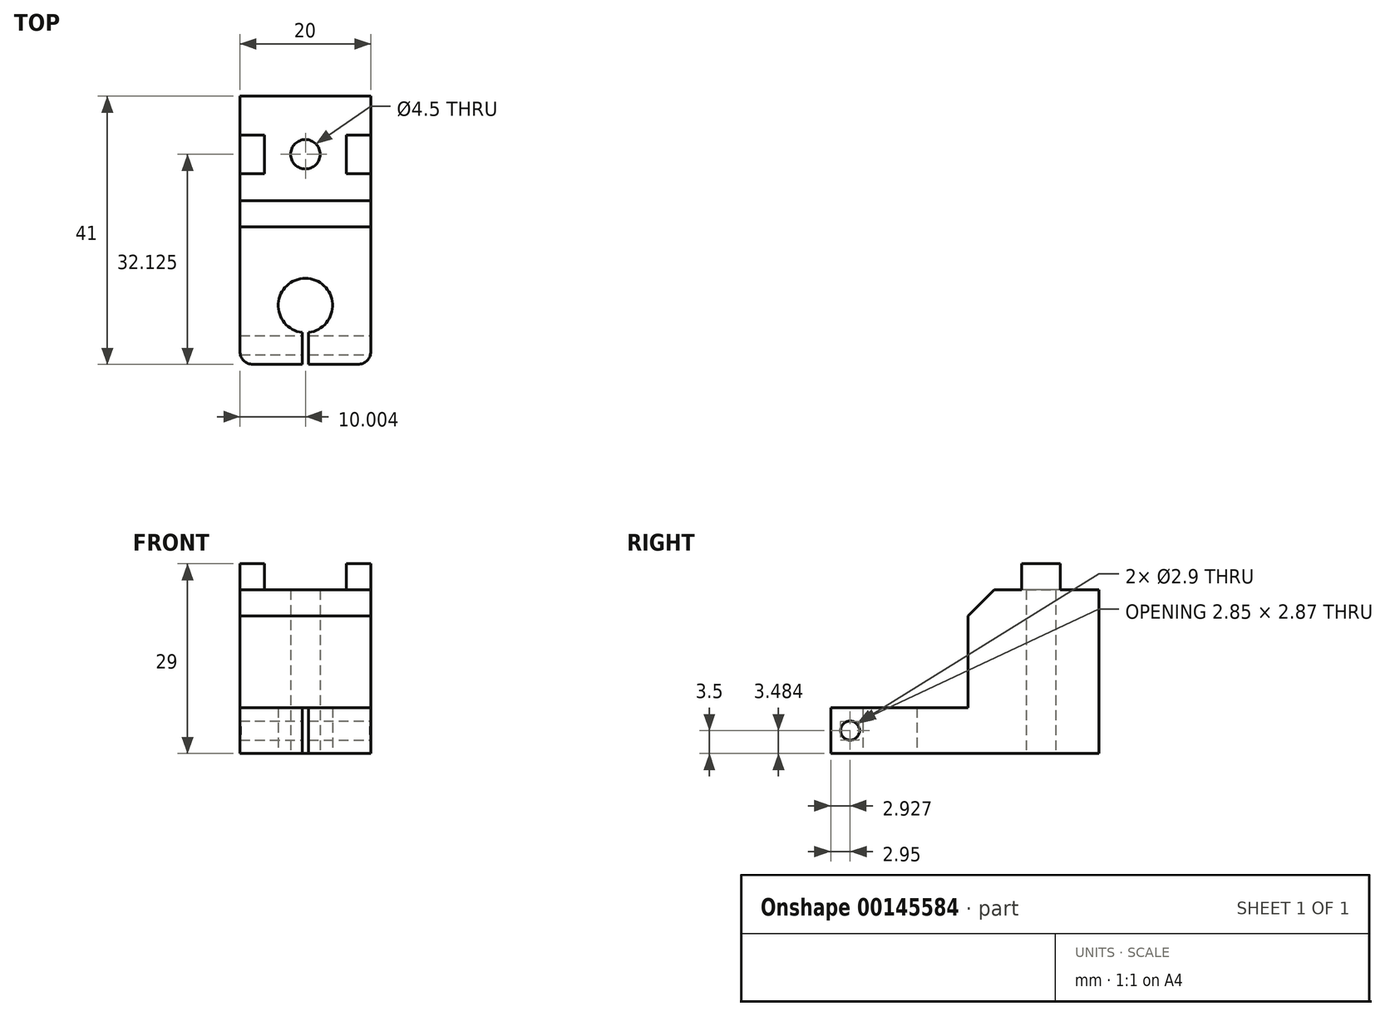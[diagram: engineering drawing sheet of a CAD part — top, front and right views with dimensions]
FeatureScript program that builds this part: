
annotation { "Feature Type Name" : "Feature", "Feature Type Description" : "" }
export const myFeature = defineFeature(function(context is Context, id is Id, definition is map)
    precondition{}
    {
        {
            var Q0;
            Q0=qCreatedBy(makeId("Top.planeOp"),FACE);
            var sketch = newSketch(context, id + "F0", { "sketchPlane" : qUnion([Q0])});
            skLineSegment(sketch, "E0.bottom", {"start": v(-6.6, 0) * mm, "end": v(13.4, 0) * mm});
            skLineSegment(sketch, "E0.top", {"start": v(-6.6, 41) * mm, "end": v(13.4, 41) * mm});
            skLineSegment(sketch, "E0.left", {"start": v(-6.6, 0) * mm, "end": v(-6.6, 41) * mm});
            skLineSegment(sketch, "E0.right", {"start": v(13.4, 0) * mm, "end": v(13.4, 41) * mm});
            skLineSegment(sketch, "E1", {"start": v(-6.6, 21) * mm, "end": v(13.4, 21) * mm, "construction": true});
            skPoint(sketch, "E2.centerSnap0", {"position": v(3.4, 41) * mm});
            skCircle(sketch, "E3", {"center": v(3.4, 9) * mm, "radius": 4.15 * mm});
            skLineSegment(sketch, "E4.bottom", {"start": v(3.9, 0) * mm, "end": v(2.9, 0) * mm});
            skLineSegment(sketch, "E4.top", {"start": v(3.9, 9) * mm, "end": v(2.9, 9) * mm});
            skLineSegment(sketch, "E4.left", {"start": v(3.9, 0) * mm, "end": v(3.9, 9) * mm});
            skLineSegment(sketch, "E4.right", {"start": v(2.9, 0) * mm, "end": v(2.9, 9) * mm});
            skArc(sketch, "E5", {"start": v(5.65, 32.12) * mm, "mid": v(3.4, 34.38) * mm, "end": v(1.15, 32.12) * mm});
            skLineSegment(sketch, "E6", {"start": v(-6.6, 21) * mm, "end": v(13.4, 21) * mm});
            skArc(sketch, "E7", {"start": v(1.15, 32.12) * mm, "mid": v(3.4, 29.88) * mm, "end": v(5.65, 32.12) * mm});
            skLineSegment(sketch, "E8.bottom", {"start": v(-6.6, 35.08) * mm, "end": v(-2.85, 35.08) * mm});
            skLineSegment(sketch, "E8.top", {"start": v(-6.6, 29.18) * mm, "end": v(-2.85, 29.18) * mm});
            skLineSegment(sketch, "E8.left", {"start": v(-6.6, 35.08) * mm, "end": v(-6.6, 29.18) * mm});
            skLineSegment(sketch, "E8.right", {"start": v(-2.85, 35.07) * mm, "end": v(-2.85, 29.17) * mm});
            skLineSegment(sketch, "E9.bottom", {"start": v(13.4, 35.08) * mm, "end": v(9.65, 35.08) * mm});
            skLineSegment(sketch, "E9.top", {"start": v(13.4, 29.18) * mm, "end": v(9.65, 29.18) * mm});
            skLineSegment(sketch, "E9.left", {"start": v(13.4, 35.08) * mm, "end": v(13.4, 29.17) * mm});
            skLineSegment(sketch, "E9.right", {"start": v(9.65, 35.07) * mm, "end": v(9.65, 29.17) * mm});
            skPoint(sketch, "E10", {"position": v(-2.85, 32.12) * mm});
            skSolve(sketch);
        }
        {
            var Q0;
            Q0=makeQuery(id+"F0.imprint","IMPRINT",FACE,{"disambiguationData":[TD([[makeQuery(id+"F0.imprint","IMPRINT",EDGE,{"derivedFrom":sQuery(id+"F0.wireOp",EDGE,"E0.top")}),-1.0]])]});
            var Q1;
            {var subQ1=sQuery(id+"F0.wireOp",EDGE,"E0.bottom");var subQ5=sQuery(id+"F0.wireOp",EDGE,"E0.left");var subQ6=makeQuery(id+"F0.imprint","INTERSECT",VERTEX,{"derivedFrom":[subQ1,subQ5]});Q1=makeQuery(id+"F0.imprint","IMPRINT",FACE,{"disambiguationData":[TD([[makeQuery(id+"F0.imprint","IMPRINT",EDGE,{"disambiguationData":[TD([[subQ6,-1.0]])],"derivedFrom":subQ5}),-1.0]])]});}
            var Q2;
            {var subQ0=sQuery(id+"F0.wireOp",EDGE,"E4.left");var subQ1=sQuery(id+"F0.wireOp",EDGE,"E3");var subQ2=makeQuery(id+"F0.imprint","INTERSECT",VERTEX,{"derivedFrom":[subQ1,subQ0]});Q2=makeQuery(id+"F0.imprint","IMPRINT",FACE,{"disambiguationData":[TD([[makeQuery(id+"F0.imprint","IMPRINT",EDGE,{"disambiguationData":[TD([[subQ2,-1.0]])],"derivedFrom":subQ1}),-1.0]])]});}
            var Q3;
            Q3 = qSketchRegion(id + "F2", true);
            extrude(context, id + "F1", {"entities" : qUnion([Q0, Q1, Q2, Q3]), "depth" : 7 * mm});
        }
        {
            var Q0;
            Q0=makeQuery(id+"FQucasgnR9fUPlY_1.boolean.opBoolean","MERGE",FACE,{"derivedFrom":[makeQuery(id+"F1.opExtrude","SWEPT_FACE",FACE,{"disambiguationData":[OSD([sQuery(id+"F0.wireOp",EDGE,"E0.right")])]}),makeQuery(id+"FQucasgnR9fUPlY_1.opExtrude","SWEPT_FACE",FACE,{"disambiguationData":[OSD([sQuery(id+"Fag0aYCVP3Ujfj8_1.wireOp",EDGE,"1siYL01j-m5db-GpVy-yTCy-yeia6Dgr4sKR.left")])]})]});
            var sketch = newSketch(context, id + "F2", { "sketchPlane" : qUnion([Q0])});
            skCircle(sketch, "E11", {"center": v(2.95, 3.5) * mm, "radius": 1.45 * mm});
            skPoint(sketch, "E11.centerSnap0", {"position": v(0, 3.5) * mm});
            skSolve(sketch);
        }
        {
            var Q0;
            Q0=qSketchRegion(id+"F2",true);
            extrude(context, id + "F3", {"entities" : qUnion([Q0]), "operationType" : NewBodyOperationType.REMOVE, "oppositeDirection" : true, "depth" : 25 * mm});
        }
        {
            var Q0;
            Q0=makeQuery(id+"F1.opExtrude","SWEPT_EDGE",EDGE,{"disambiguationData":[OSD([sQuery(id+"F0.wireOp",EDGE,"E0.bottom"),sQuery(id+"F0.wireOp",EDGE,"E0.right")])]});
            var Q1;
            Q1=makeQuery(id+"F1.opExtrude","SWEPT_EDGE",EDGE,{"disambiguationData":[OSD([sQuery(id+"F0.wireOp",EDGE,"E0.bottom"),sQuery(id+"F0.wireOp",EDGE,"E0.left")])]});
            var Q2;
            Q2=makeQuery(id+"F1.opExtrude","SWEPT_EDGE",EDGE,{"disambiguationData":[OSD([sQuery(id+"F0.wireOp",EDGE,"E0.top"),sQuery(id+"F0.wireOp",EDGE,"E0.right")])]});
            var Q3;
            Q3=makeQuery(id+"F1.opExtrude","SWEPT_EDGE",EDGE,{"disambiguationData":[OSD([sQuery(id+"F0.wireOp",EDGE,"E0.top"),sQuery(id+"F0.wireOp",EDGE,"E0.left")])]});
            var Q4;
            Q4=makeQuery(id+"FxEKCNikidz0gRl_1.opExtrude","SWEPT_EDGE",EDGE,{"disambiguationData":[OSD([sQuery(id+"F0.wireOp",EDGE,"E0.left"),sQuery(id+"F0.wireOp",EDGE,"E6")])]});
            var Q5;
            Q5=makeQuery(id+"FxEKCNikidz0gRl_1.opExtrude","SWEPT_EDGE",EDGE,{"disambiguationData":[OSD([sQuery(id+"F0.wireOp",EDGE,"E0.right"),sQuery(id+"F0.wireOp",EDGE,"E6")])]});
            fillet(context, id + "F4", {"entities" : qUnion([Q0, Q1, Q2, Q3, Q4, Q5]), "radius" : 2 * mm, "tangentPropagation" : true, "allowEdgeOverflow" : false});
        }
        {
            var Q0;
            {var subQ0=sQuery(id+"F0.wireOp",EDGE,"3FrZSwRx-BHYU-xFG2-6Kof-1uWE4lx33m1z");Q0=makeQuery(id+"F0.imprint","IMPRINT",FACE,{"disambiguationData":[TD([[makeQuery(id+"F0.imprint","IMPRINT",EDGE,{"derivedFrom":subQ0}),-1.0]])]});}
            var Q1;
            {var subQ0=sQuery(id+"F0.wireOp",EDGE,"3FrZSwRx-BHYU-xFG2-6Kof-1uWE4lx33m1z");Q1=makeQuery(id+"F0.imprint","IMPRINT",FACE,{"disambiguationData":[TD([[makeQuery(id+"F0.imprint","IMPRINT",EDGE,{"derivedFrom":subQ0}),1.0]])]});}
            var Q2;
            {var subQ11=sQuery(id+"F0.wireOp",EDGE,"E9.bottom");Q2=makeQuery(id+"F0.imprint","IMPRINT",FACE,{"disambiguationData":[TD([[makeQuery(id+"F0.imprint","IMPRINT",EDGE,{"derivedFrom":subQ11}),-1.0]])]});}
            var Q3;
            {var subQ9=sQuery(id+"F0.wireOp",EDGE,"E8.bottom");Q3=makeQuery(id+"F0.imprint","IMPRINT",FACE,{"disambiguationData":[TD([[makeQuery(id+"F0.imprint","IMPRINT",EDGE,{"derivedFrom":subQ9}),1.0]])]});}
            extrude(context, id + "F5", {"entities" : qUnion([Q0, Q1, Q2, Q3]), "operationType" : NewBodyOperationType.ADD, "depth" : 25 * mm});
        }
        {
            var Q0;
            Q0=makeQuery(id+"F0.imprint","IMPRINT",FACE,{"disambiguationData":[TD([[makeQuery(id+"F0.imprint","IMPRINT",EDGE,{"derivedFrom":sQuery(id+"F0.wireOp",EDGE,"E8.bottom")}),-1.0]])]});
            var Q1;
            Q1=makeQuery(id+"F0.imprint","IMPRINT",FACE,{"disambiguationData":[TD([[makeQuery(id+"F0.imprint","IMPRINT",EDGE,{"derivedFrom":sQuery(id+"F0.wireOp",EDGE,"E9.bottom")}),1.0]])]});
            extrude(context, id + "F6", {"entities" : qUnion([Q0, Q1]), "operationType" : NewBodyOperationType.ADD, "depth" : 29 * mm});
        }
        {
            var Q0;
            Q0=makeQuery(id+"F5.opExtrude","CAP_EDGE",EDGE,{"disambiguationData":[OSD([sQuery(id+"F0.wireOp",EDGE,"E6")])],"isStart":false});
            chamfer(context, id + "F7", {"entities" : qUnion([Q0]), "width" : 4 * mm, "tangentPropagation" : true});
        }
    });
